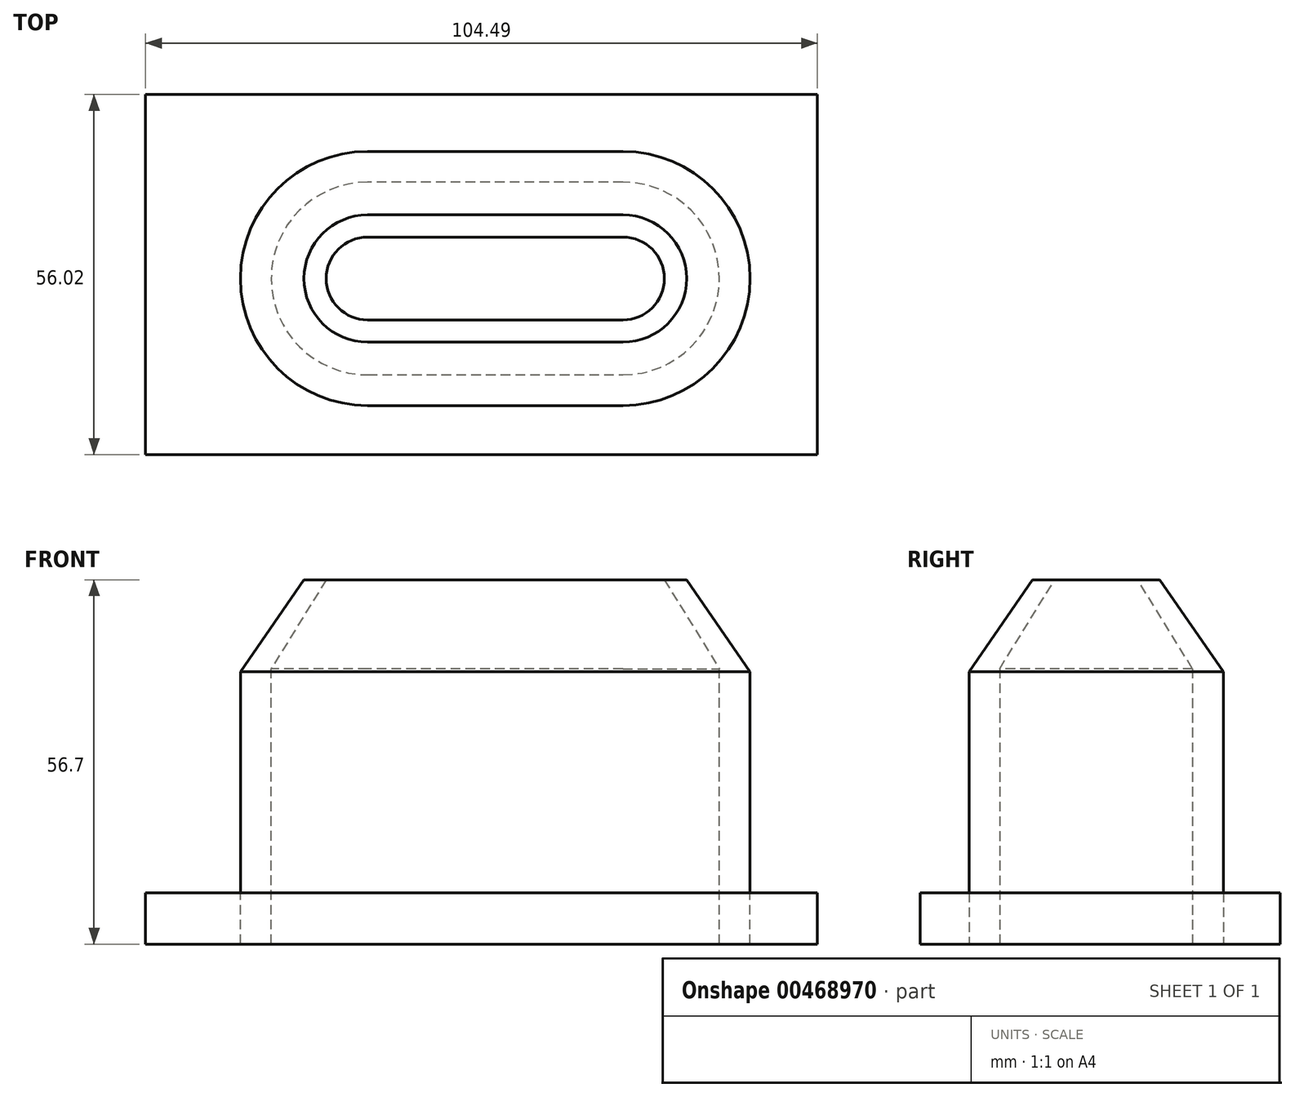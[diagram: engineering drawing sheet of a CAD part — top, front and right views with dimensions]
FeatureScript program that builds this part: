
annotation { "Feature Type Name" : "Feature", "Feature Type Description" : "" }
export const myFeature = defineFeature(function(context is Context, id is Id, definition is map)
    precondition{}
    {
        {
            var Q0;
            Q0=qCreatedBy(makeId("Top.planeOp"),FACE);
            var sketch = newSketch(context, id + "F0", { "sketchPlane" : qUnion([Q0])});
            skLineSegment(sketch, "E0", {"start": v(0, 30) * mm, "end": v(-19.86, 30) * mm});
            skArc(sketch, "E1", {"start": v(-19.86, 30) * mm, "mid": v(-34.86, 15) * mm, "end": v(-19.86, 0) * mm});
            skLineSegment(sketch, "E2", {"start": v(-19.86, 0) * mm, "end": v(0, 0) * mm});
            skLineSegment(sketch, "E3", {"start": v(0, 30) * mm, "end": v(0, 0) * mm, "construction": true});
            skLineSegment(sketch, "E4.MirrorCS", {"start": v(0, 30) * mm, "end": v(19.86, 30) * mm});
            skLineSegment(sketch, "E5.MirrorCS", {"start": v(19.86, 0) * mm, "end": v(0, 0) * mm});
            skArc(sketch, "E6.MirrorCS", {"start": v(19.86, 30) * mm, "mid": v(34.86, 15) * mm, "end": v(19.86, 0) * mm});
            skSolve(sketch);
        }
        {
            var Q0;
            Q0=qCreatedBy(makeId("Right.planeOp"),FACE);
            var sketch = newSketch(context, id + "F1", { "sketchPlane" : qUnion([Q0])});
            skLineSegment(sketch, "E7", {"start": v(0, 42.87) * mm, "end": v(8.55, 56.7) * mm});
            skLineSegment(sketch, "E8", {"start": v(8.55, 56.7) * mm, "end": v(5.1, 56.7) * mm});
            skLineSegment(sketch, "E9", {"start": v(5.1, 56.7) * mm, "end": v(-4.78, 42.37) * mm});
            skLineSegment(sketch, "E10", {"start": v(-4.78, 42.37) * mm, "end": v(-4.78, 0) * mm});
            skLineSegment(sketch, "E11", {"start": v(-4.78, 0) * mm, "end": v(0, 0) * mm});
            skLineSegment(sketch, "E12", {"start": v(0, 42.87) * mm, "end": v(0, 0) * mm});
            skSolve(sketch);
        }
        {
            var Q0;
            Q0=makeQuery(id+"F1.imprint","IMPRINT",FACE,{"disambiguationData":[TD([[makeQuery(id+"F1.imprint","IMPRINT",EDGE,{"derivedFrom":sQuery(id+"F1.wireOp",EDGE,"E7")}),1.0]])]});
            var Q1;
            Q1=sQuery(id+"F0.wireOp",EDGE,"E2");
            var Q2;
            Q2=sQuery(id+"F0.wireOp",EDGE,"E1");
            var Q3;
            Q3=sQuery(id+"F0.wireOp",EDGE,"E0");
            var Q4;
            Q4=sQuery(id+"F0.wireOp",EDGE,"E4.MirrorCS");
            var Q5;
            Q5=sQuery(id+"F0.wireOp",EDGE,"E6.MirrorCS");
            var Q6;
            Q6=sQuery(id+"F0.wireOp",EDGE,"E5.MirrorCS");
            sweep(context, id + "F2", {"profiles" : qUnion([Q0]), "path" : qUnion([Q1, Q2, Q3, Q4, Q5, Q6])});
        }
        {
            var Q0;
            Q0=qCreatedBy(makeId("Top.planeOp"),FACE);
            var sketch = newSketch(context, id + "F3", { "sketchPlane" : qUnion([Q0])});
            skLineSegment(sketch, "E13.bottom", {"start": v(-54.4, -12.39) * mm, "end": v(50.09, -12.39) * mm});
            skLineSegment(sketch, "E13.top", {"start": v(-54.4, 43.63) * mm, "end": v(50.09, 43.63) * mm});
            skLineSegment(sketch, "E13.left", {"start": v(-54.4, -12.39) * mm, "end": v(-54.4, 43.63) * mm});
            skLineSegment(sketch, "E13.right", {"start": v(50.09, -12.39) * mm, "end": v(50.09, 43.63) * mm});
            skSolve(sketch);
        }
        {
            var Q0;
            Q0=makeQuery(id+"F3.imprint","IMPRINT",FACE,{"disambiguationData":[TD([[makeQuery(id+"F3.imprint","IMPRINT",EDGE,{"derivedFrom":sQuery(id+"F3.wireOp",EDGE,"E13.bottom")}),1.0]])]});
            extrude(context, id + "F4", {"entities" : qUnion([Q0]), "depth" : 8 * mm, "offsetDistance" : 25 * mm});
        }
    });
